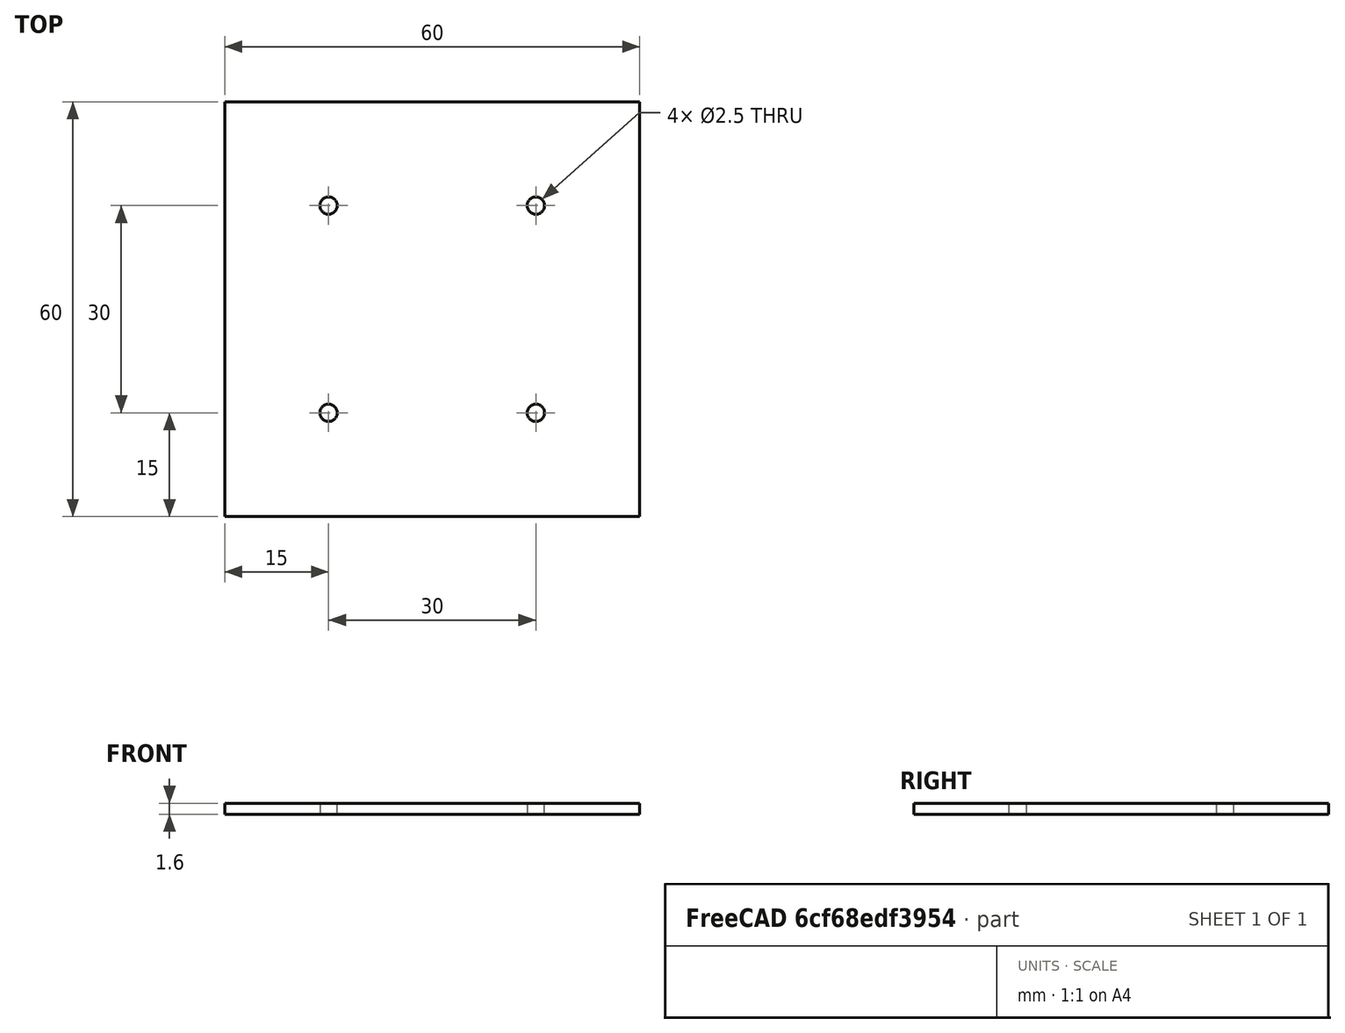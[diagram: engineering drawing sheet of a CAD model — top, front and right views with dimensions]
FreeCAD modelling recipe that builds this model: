
FCSTD DOCUMENT  (FreeCAD 0.20R29177 (Git))
Label: PCB
License: All rights reserved
LicenseURL: http://en.wikipedia.org/wiki/All_rights_reserved
objects: Sketcher::SketchObject×1, PartDesign::Pad×1, PartDesign::Body×1
note: 4 computed .brp shape members not serialized (recipe doc carries the construction recipe); baked Part::Feature solids carry a one-line shape summary decoded from their .brp

FEATURE [Sketcher::SketchObject] Sketch
  FullyConstrained = true
  MapMode = 5
  Support = -> [XY_Plane]
  sketch-geometry (10):
    g0: LineSegment StartX=-30 StartY=30 StartZ=0 EndX=30 EndY=30 EndZ=0
    g1: LineSegment StartX=30 StartY=30 StartZ=0 EndX=30 EndY=-30 EndZ=0
    g2: LineSegment StartX=30 StartY=-30 StartZ=0 EndX=-30 EndY=-30 EndZ=0
    g3: LineSegment StartX=-30 StartY=-30 StartZ=0 EndX=-30 EndY=30 EndZ=0
    g4: Circle CenterX=-15 CenterY=-15 CenterZ=0 NormalX=0 NormalY=0 NormalZ=1 AngleXU=0 Radius=1.25
    g5: Circle CenterX=-15 CenterY=15 CenterZ=0 NormalX=0 NormalY=0 NormalZ=1 AngleXU=0 Radius=1.25
    g6: Circle CenterX=15 CenterY=15 CenterZ=0 NormalX=0 NormalY=0 NormalZ=1 AngleXU=0 Radius=1.25
    g7: Circle CenterX=15 CenterY=-15 CenterZ=0 NormalX=0 NormalY=0 NormalZ=1 AngleXU=0 Radius=1.25
    g8: LineSegment StartX=-15 StartY=15 StartZ=0 EndX=-15 EndY=-15 EndZ=0
    g9: LineSegment StartX=-15 StartY=-15 StartZ=0 EndX=15 EndY=-15 EndZ=0
  constraints (24):
    c: Coincident(g0,g1)
    c: Coincident(g1,g2)
    c: Coincident(g2,g3)
    c: Coincident(g3,g0)
    c: Horizontal(g0)
    c: Horizontal(g2)
    c: Vertical(g1)
    c: Vertical(g3)
    c: Equal(g0,g1)
    c: Symmetric(g0,g2,g-1)
    c: DistanceY(g1,g1) = 60
    c: Equal(g7,g4)
    c: Equal(g7,g5)
    c: Equal(g7,g6)
    c: Diameter(g7) = 2.5
    c: Symmetric(g5,g6,g-2)
    c: Symmetric(g7,g4,g-2)
    c: Symmetric(g4,g5,g-1)
    c: Coincident(g8,g5)
    c: Coincident(g8,g4)
    c: Coincident(g8,g9)
    c: Coincident(g9,g7)
    c: Equal(g9,g8)
    c: DistanceY(g4,g-1) = 15
FEATURE [PartDesign::Pad] Pad
  Direction = (0,0,1)
  Length = 1.6
  Length2 = 10
  Profile = -> Sketch
  ReferenceAxis = -> Sketch [N_Axis]
  Type = 0
FEATURE [PartDesign::Body] Body  label="PCB"
  Group = -> [Sketch,Pad]
  Origin = -> Origin
  Tip = -> Pad
